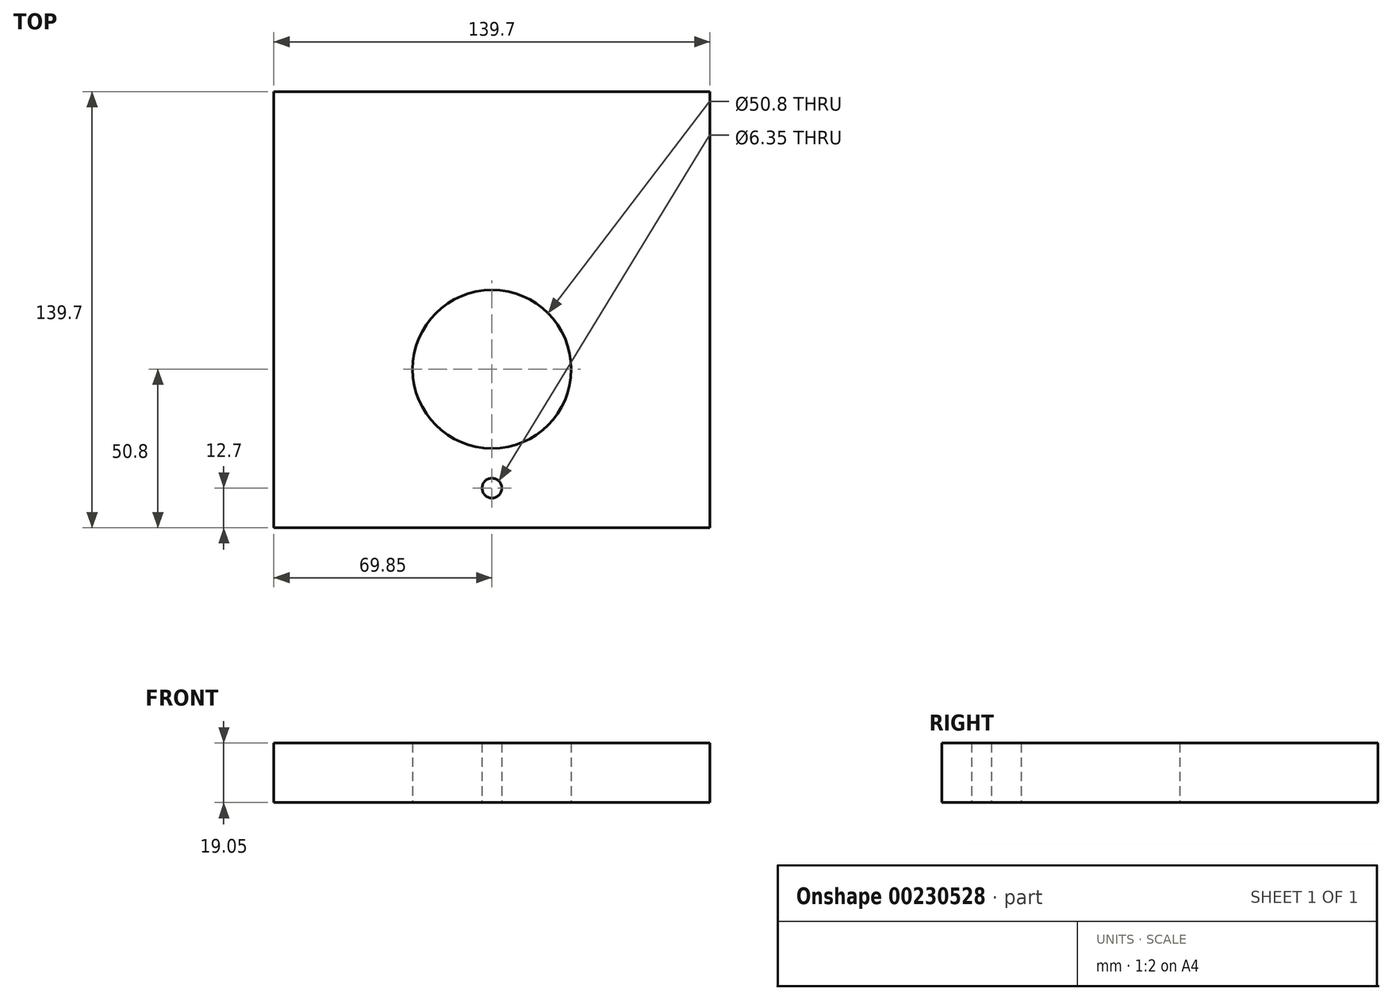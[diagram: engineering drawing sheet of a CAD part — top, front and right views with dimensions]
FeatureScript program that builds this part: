
annotation { "Feature Type Name" : "Feature", "Feature Type Description" : "" }
export const myFeature = defineFeature(function(context is Context, id is Id, definition is map)
    precondition{}
    {
        {
            var Q0;
            Q0=qCreatedBy(makeId("Top.planeOp"),FACE);
            var sketch = newSketch(context, id + "F0", { "sketchPlane" : qUnion([Q0])});
            skLineSegment(sketch, "E0.bottom", {"start": v(-69.85, -69.85) * mm, "end": v(69.85, -69.85) * mm});
            skLineSegment(sketch, "E0.top", {"start": v(-69.85, 69.85) * mm, "end": v(69.85, 69.85) * mm});
            skLineSegment(sketch, "E0.left", {"start": v(-69.85, -69.85) * mm, "end": v(-69.85, 69.85) * mm});
            skLineSegment(sketch, "E0.right", {"start": v(69.85, -69.85) * mm, "end": v(69.85, 69.85) * mm});
            skPoint(sketch, "E0.middle", {"position": v(0, 0) * mm});
            skCircle(sketch, "E1", {"center": v(0, -19.05) * mm, "radius": 25.4 * mm});
            skCircle(sketch, "E2", {"center": v(0, -57.15) * mm, "radius": 3.18 * mm});
            skSolve(sketch);
        }
        {
            var Q0;
            Q0=makeQuery(id+"F0.imprint","IMPRINT",FACE,{"disambiguationData":[TD([[makeQuery(id+"F0.imprint","IMPRINT",EDGE,{"derivedFrom":sQuery(id+"F0.wireOp",EDGE,"E0.bottom")}),1.0]])]});
            extrude(context, id + "F1", {"entities" : qUnion([Q0]), "depth" : 19.05 * mm});
        }
    });
